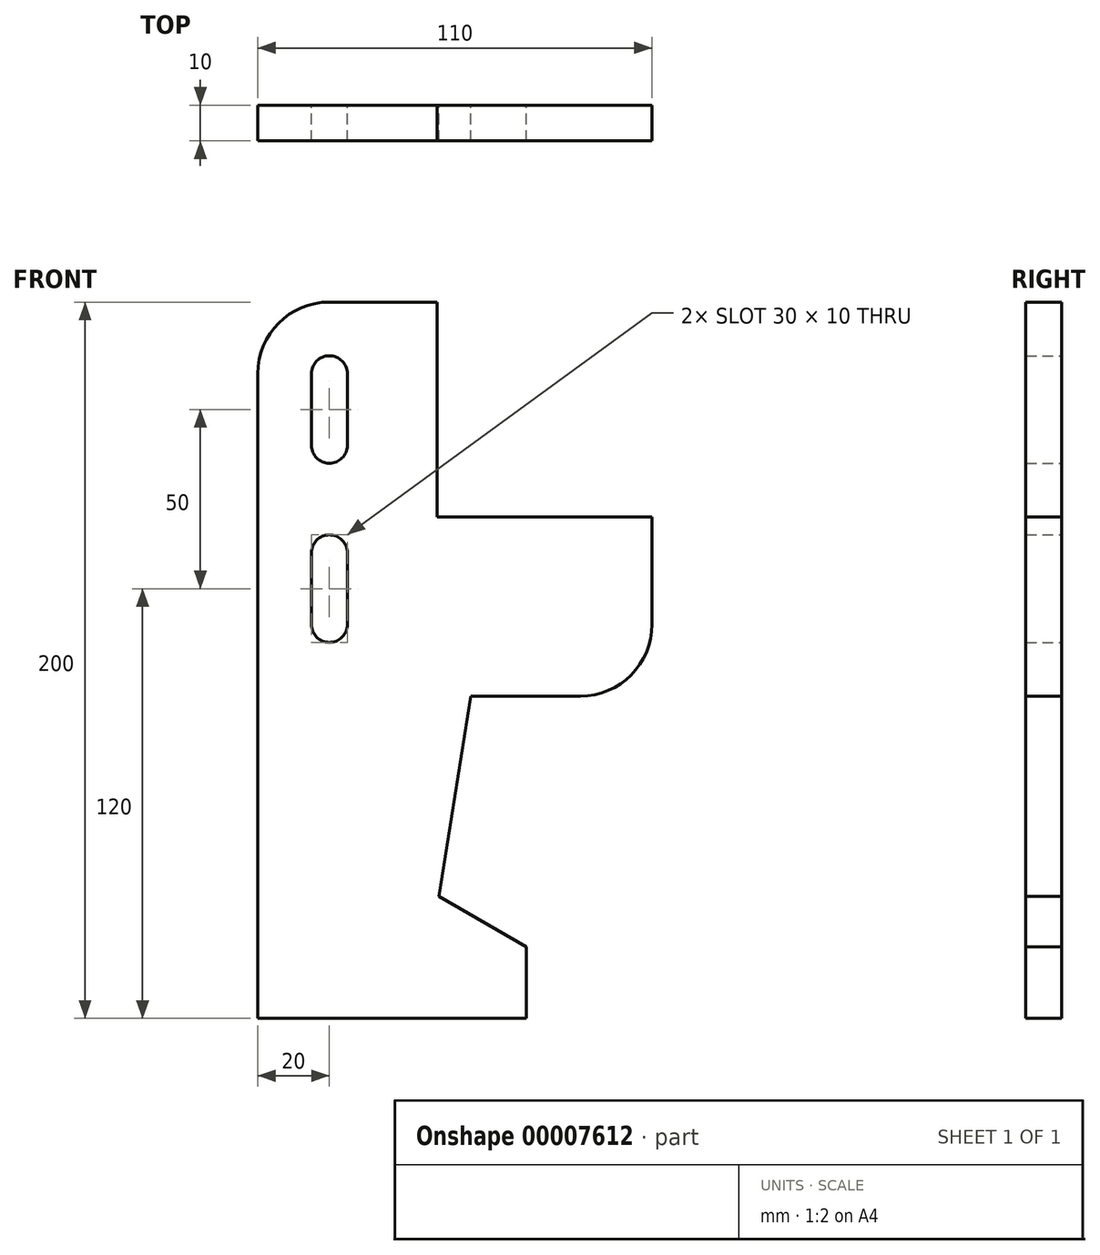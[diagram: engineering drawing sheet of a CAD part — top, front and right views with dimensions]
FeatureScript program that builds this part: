
annotation { "Feature Type Name" : "Feature", "Feature Type Description" : "" }
export const myFeature = defineFeature(function(context is Context, id is Id, definition is map)
    precondition{}
    {
        {
            var Q0;
            Q0=qCreatedBy(makeId("Front.planeOp"),FACE);
            var sketch = newSketch(context, id + "F0", { "sketchPlane" : qUnion([Q0])});
            skLineSegment(sketch, "E0", {"start": v(0, 0) * mm, "end": v(0, 60) * mm});
            skLineSegment(sketch, "E1", {"start": v(0, 60) * mm, "end": v(-30, 60) * mm});
            skLineSegment(sketch, "E2", {"start": v(-50, 40) * mm, "end": v(-50, -140) * mm});
            skLineSegment(sketch, "E3", {"start": v(-50, -140) * mm, "end": v(25, -140) * mm});
            skLineSegment(sketch, "E4", {"start": v(25, -140) * mm, "end": v(25, -120) * mm});
            skLineSegment(sketch, "E5", {"start": v(25, -120) * mm, "end": v(0.6, -105.9) * mm});
            skLineSegment(sketch, "E6", {"start": v(0.6, -105.9) * mm, "end": v(9.45, -50) * mm});
            skLineSegment(sketch, "E7", {"start": v(9.45, -50) * mm, "end": v(40, -50) * mm});
            skLineSegment(sketch, "E8", {"start": v(60, -30) * mm, "end": v(60, 0) * mm});
            skLineSegment(sketch, "E9", {"start": v(60, 0) * mm, "end": v(0, 0) * mm});
            skPoint(sketch, "E10.visualSharp", {"position": v(-50, 60) * mm});
            skArc(sketch, "E10.filletArc", {"start": v(-30, 60) * mm, "mid": v(-44.14, 54.14) * mm, "end": v(-50, 40) * mm});
            skPoint(sketch, "E11.visualSharp", {"position": v(60, -50) * mm});
            skArc(sketch, "E11.filletArc", {"start": v(40, -50) * mm, "mid": v(54.14, -44.14) * mm, "end": v(60, -30) * mm});
            skLineSegment(sketch, "E12", {"start": v(-35, 40) * mm, "end": v(-35, 20) * mm});
            skArc(sketch, "E13", {"start": v(-35, 20) * mm, "mid": v(-30, 15) * mm, "end": v(-25, 20) * mm});
            skLineSegment(sketch, "E14", {"start": v(-25, 20) * mm, "end": v(-25, 40) * mm});
            skArc(sketch, "E15", {"start": v(-25, 40) * mm, "mid": v(-30, 45) * mm, "end": v(-35, 40) * mm});
            skLineSegment(sketch, "E16.0.1.0", {"start": v(-25, -30) * mm, "end": v(-25, -10) * mm});
            skLineSegment(sketch, "E16.0.1.1", {"start": v(-35, -10) * mm, "end": v(-35, -30) * mm});
            skArc(sketch, "E16.0.1.2", {"start": v(-25, -10) * mm, "mid": v(-30, -5) * mm, "end": v(-35, -10) * mm});
            skArc(sketch, "E16.0.1.3", {"start": v(-35, -30) * mm, "mid": v(-30, -35) * mm, "end": v(-25, -30) * mm});
            skLineSegment(sketch, "E16.direction1", {"start": v(-25, 20) * mm, "end": v(0, 20) * mm, "construction": true});
            skLineSegment(sketch, "E16.direction2", {"start": v(-25, 20) * mm, "end": v(-25, -30) * mm, "construction": true});
            skSolve(sketch);
        }
        {
            var Q0;
            Q0 = qSketchRegion(id + "F0", true);
            extrude(context, id + "F1", {"entities" : qUnion([Q0]), "endBound" : BoundingType.SYMMETRIC, "depth" : 10 * mm});
        }
    });
